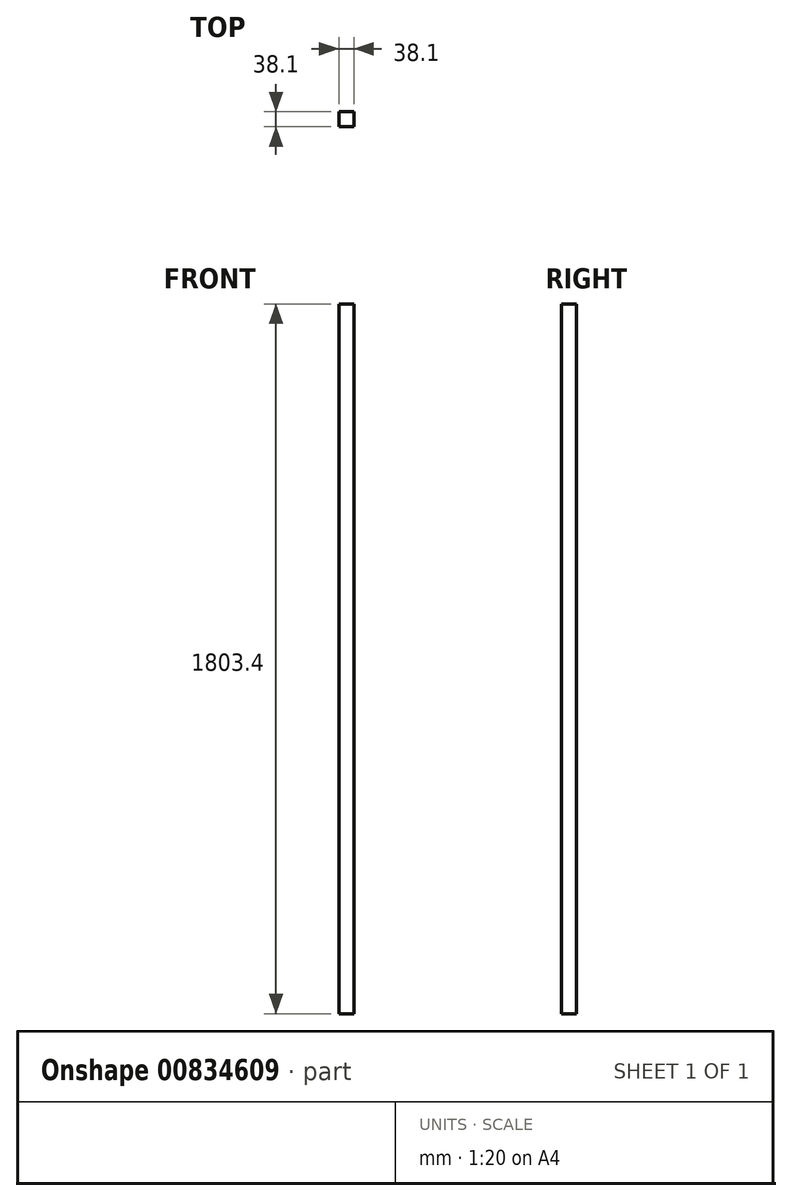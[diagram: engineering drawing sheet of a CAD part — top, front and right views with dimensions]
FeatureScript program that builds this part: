
annotation { "Feature Type Name" : "Feature", "Feature Type Description" : "" }
export const myFeature = defineFeature(function(context is Context, id is Id, definition is map)
    precondition{}
    {
        {
            var Q0;
            Q0=qCreatedBy(makeId("Top.planeOp"),FACE);
            var sketch = newSketch(context, id + "F0", { "sketchPlane" : qUnion([Q0])});
            skLineSegment(sketch, "E0.bottom", {"start": v(19.05, 19.05) * mm, "end": v(-19.05, 19.05) * mm});
            skLineSegment(sketch, "E0.top", {"start": v(19.05, -19.05) * mm, "end": v(-19.05, -19.05) * mm});
            skLineSegment(sketch, "E0.left", {"start": v(19.05, 19.05) * mm, "end": v(19.05, -19.05) * mm});
            skLineSegment(sketch, "E0.right", {"start": v(-19.05, 19.05) * mm, "end": v(-19.05, -19.05) * mm});
            skPoint(sketch, "E0.middle", {"position": v(0, 0) * mm});
            skSolve(sketch);
        }
        {
            var Q0;
            Q0=qSketchRegion(id+"F0",true);
            extrude(context, id + "F1", {"entities" : qUnion([Q0]), "oppositeDirection" : true, "depth" : 1803.4 * mm, "offsetDistance" : 25.4 * mm});
        }
    });
